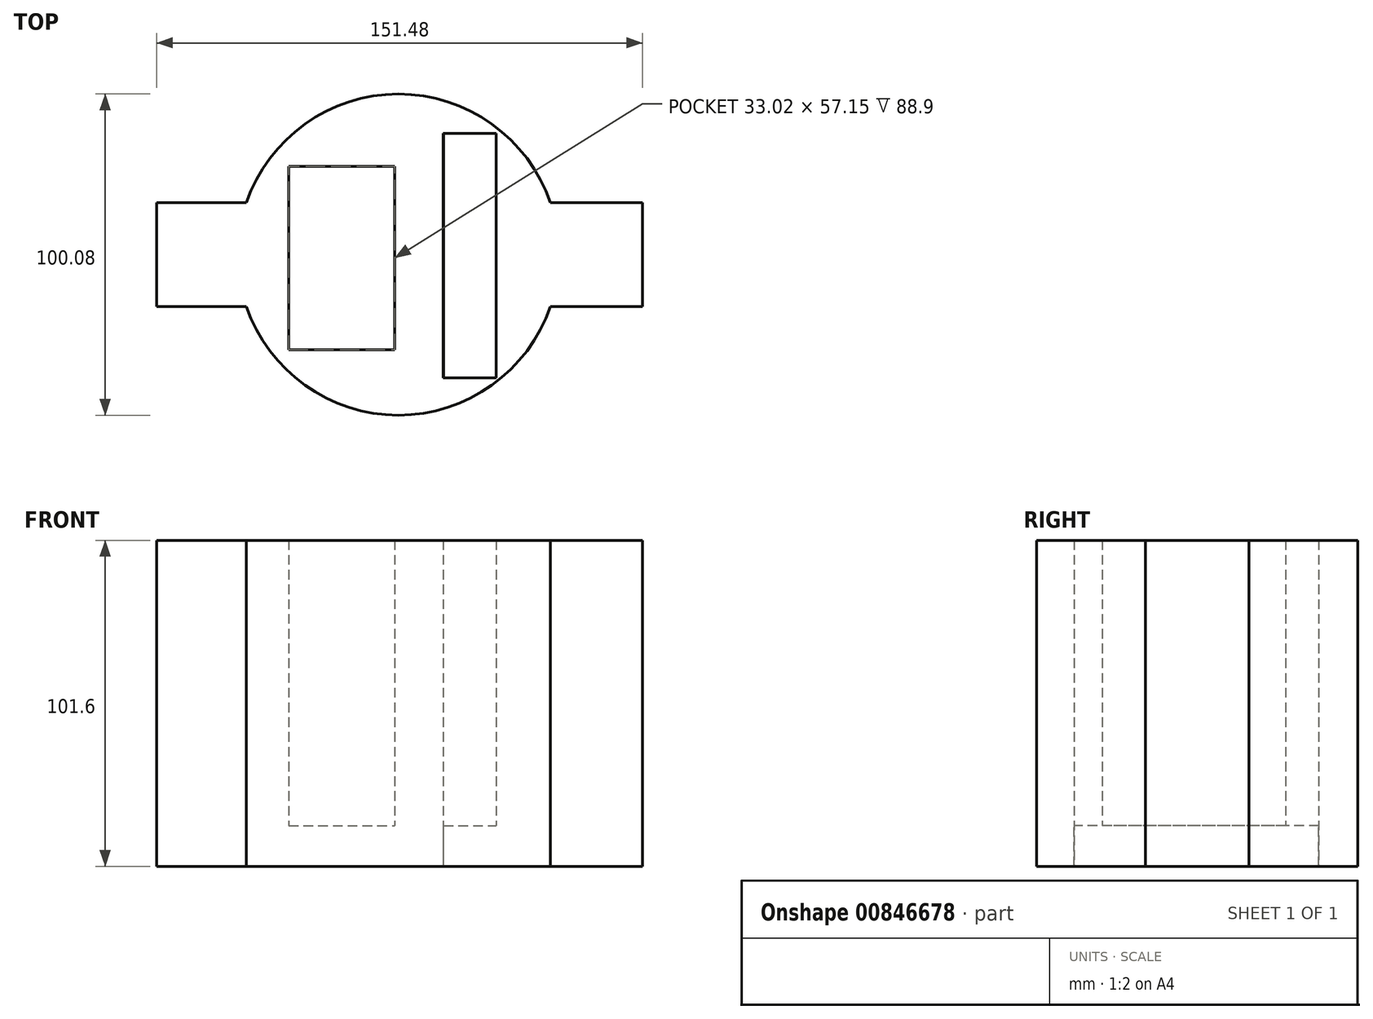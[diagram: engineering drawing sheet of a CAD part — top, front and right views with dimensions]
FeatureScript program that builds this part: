
annotation { "Feature Type Name" : "Feature", "Feature Type Description" : "" }
export const myFeature = defineFeature(function(context is Context, id is Id, definition is map)
    precondition{}
    {
        {
            var Q0;
            Q0=qCreatedBy(makeId("Top.planeOp"),FACE);
            var sketch = newSketch(context, id + "F0", { "sketchPlane" : qUnion([Q0])});
            skArc(sketch, "E0", {"start": v(-47.37, -16.13) * mm, "mid": v(0, -50.04) * mm, "end": v(47.37, -16.13) * mm});
            skLineSegment(sketch, "E1.bottom", {"start": v(13.95, 37.83) * mm, "end": v(30.46, 37.83) * mm});
            skLineSegment(sketch, "E1.top", {"start": v(13.95, -38.37) * mm, "end": v(30.46, -38.37) * mm});
            skLineSegment(sketch, "E1.left", {"start": v(13.95, 37.83) * mm, "end": v(13.95, -38.37) * mm});
            skLineSegment(sketch, "E1.right", {"start": v(30.46, 37.83) * mm, "end": v(30.46, -38.37) * mm});
            skLineSegment(sketch, "E2.bottom", {"start": v(-34.18, 27.53) * mm, "end": v(-1.16, 27.53) * mm});
            skLineSegment(sketch, "E2.top", {"start": v(-34.18, -29.62) * mm, "end": v(-1.16, -29.62) * mm});
            skLineSegment(sketch, "E2.left", {"start": v(-34.18, 27.53) * mm, "end": v(-34.18, -29.62) * mm});
            skLineSegment(sketch, "E2.right", {"start": v(-1.16, 27.53) * mm, "end": v(-1.16, -29.62) * mm});
            skLineSegment(sketch, "E3.bottom", {"start": v(-75.37, 16.13) * mm, "end": v(-47.37, 16.13) * mm});
            skLineSegment(sketch, "E3.top", {"start": v(-75.37, -16.13) * mm, "end": v(-47.37, -16.13) * mm});
            skLineSegment(sketch, "E3.left", {"start": v(-75.37, 16.13) * mm, "end": v(-75.37, -16.13) * mm});
            skLineSegment(sketch, "E3.right", {"start": v(76.11, 16.13) * mm, "end": v(76.11, -16.13) * mm});
            skArc(sketch, "E4.trimOffspring", {"start": v(47.37, 16.13) * mm, "mid": v(0, 50.04) * mm, "end": v(-47.37, 16.13) * mm});
            skLineSegment(sketch, "E5.trimOffspring", {"start": v(47.37, 16.13) * mm, "end": v(76.11, 16.13) * mm});
            skLineSegment(sketch, "E6.trimOffspring", {"start": v(47.37, -16.13) * mm, "end": v(76.11, -16.13) * mm});
            skLineSegment(sketch, "E7.right", {"start": v(19.11, -37.42) * mm, "end": v(18.85, -38.37) * mm});
            skLineSegment(sketch, "E8.bottom", {"start": v(-8.11, -29.62) * mm, "end": v(0, -29.62) * mm});
            skPoint(sketch, "E9.orphan", {"position": v(13.95, -55.87) * mm});
            skLineSegment(sketch, "E10", {"start": v(47.37, -16.13) * mm, "end": v(47.37, 16.13) * mm});
            skLineSegment(sketch, "E11", {"start": v(-47.37, 16.13) * mm, "end": v(-47.37, -16.13) * mm});
            skPoint(sketch, "E7.bottom.start.orphan", {"position": v(22.2, -38.37) * mm});
            skPoint(sketch, "E8.right.end.orphan", {"position": v(0, -64.8) * mm});
            skSolve(sketch);
        }
        {
            var Q0;
            {var subQ4=sQuery(id+"F0.wireOp",EDGE,"E8.bottom");Q0=makeQuery(id+"F0.imprint","IMPRINT",FACE,{"disambiguationData":[TD([[makeQuery(id+"F0.imprint","IMPRINT",EDGE,{"derivedFrom":subQ4}),-1.0]])]});}
            var Q1;
            Q1=makeQuery(id+"F0.imprint","IMPRINT",FACE,{"disambiguationData":[TD([[makeQuery(id+"F0.imprint","IMPRINT",EDGE,{"derivedFrom":sQuery(id+"F0.wireOp",EDGE,"E7.bottom")}),1.0]])]});
            var Q2;
            Q2=makeQuery(id+"F0.imprint","IMPRINT",FACE,{"disambiguationData":[TD([[makeQuery(id+"F0.imprint","IMPRINT",EDGE,{"derivedFrom":sQuery(id+"F0.wireOp",EDGE,"E1.bottom")}),1.0]])]});
            var Q3;
            Q3=makeQuery(id+"F0.imprint","IMPRINT",FACE,{"disambiguationData":[TD([[makeQuery(id+"F0.imprint","IMPRINT",EDGE,{"derivedFrom":sQuery(id+"F0.wireOp",EDGE,"E3.bottom")}),-1.0]])]});
            var Q4;
            Q4=makeQuery(id+"F0.imprint","IMPRINT",FACE,{"disambiguationData":[TD([[makeQuery(id+"F0.imprint","IMPRINT",EDGE,{"derivedFrom":sQuery(id+"F0.wireOp",EDGE,"E3.right")}),-1.0]])]});
            extrude(context, id + "F1", {"entities" : qUnion([Q0, Q1, Q2, Q3, Q4]), "depth" : 101.6 * mm, "offsetDistance" : 25.4 * mm});
        }
        {
            var Q0;
            Q0=qCreatedBy(makeId("Top.planeOp"),FACE);
            var sketch = newSketch(context, id + "F2", { "sketchPlane" : qUnion([Q0])});
            skLineSegment(sketch, "E12.bottom", {"start": v(-34.57, 28.11) * mm, "end": v(0.1, 28.11) * mm});
            skLineSegment(sketch, "E12.top", {"start": v(-34.57, -29.96) * mm, "end": v(0.1, -29.96) * mm});
            skLineSegment(sketch, "E12.left", {"start": v(-34.57, 28.11) * mm, "end": v(-34.57, -29.96) * mm});
            skLineSegment(sketch, "E12.right", {"start": v(0.1, 28.11) * mm, "end": v(0.1, -29.96) * mm});
            skLineSegment(sketch, "E13.bottom", {"start": v(14.1, -38.8) * mm, "end": v(31.04, -38.8) * mm});
            skLineSegment(sketch, "E13.top", {"start": v(14.1, 38.59) * mm, "end": v(31.04, 38.59) * mm});
            skLineSegment(sketch, "E13.left", {"start": v(14.1, -38.8) * mm, "end": v(14.1, 38.59) * mm});
            skLineSegment(sketch, "E13.right", {"start": v(31.04, -38.8) * mm, "end": v(31.04, 38.59) * mm});
            skSolve(sketch);
        }
        {
            var Q0;
            Q0=makeQuery(id+"F2.imprint","IMPRINT",FACE,{"disambiguationData":[TD([[makeQuery(id+"F2.imprint","IMPRINT",EDGE,{"derivedFrom":sQuery(id+"F2.wireOp",EDGE,"E12.bottom")}),-1.0]])]});
            var Q1;
            Q1=makeQuery(id+"F2.imprint","IMPRINT",FACE,{"disambiguationData":[TD([[makeQuery(id+"F2.imprint","IMPRINT",EDGE,{"derivedFrom":sQuery(id+"F2.wireOp",EDGE,"E13.bottom")}),1.0]])]});
            extrude(context, id + "F3", {"entities" : qUnion([Q0, Q1]), "operationType" : NewBodyOperationType.ADD, "depth" : 12.7 * mm, "offsetDistance" : 25.4 * mm});
        }
    });
